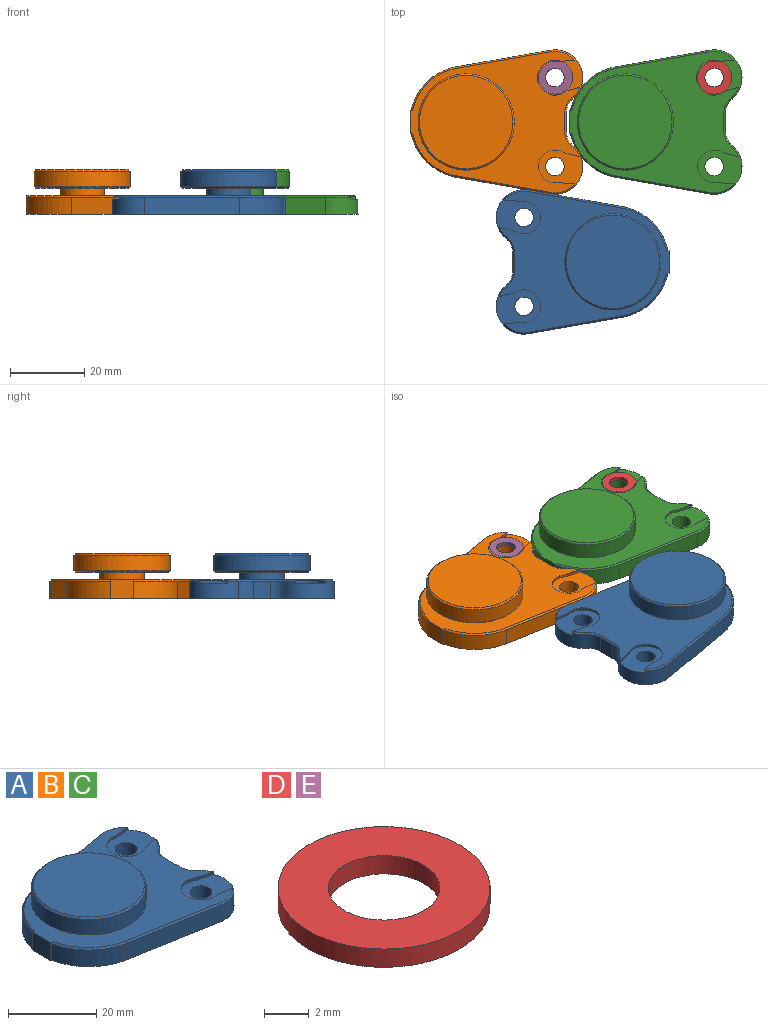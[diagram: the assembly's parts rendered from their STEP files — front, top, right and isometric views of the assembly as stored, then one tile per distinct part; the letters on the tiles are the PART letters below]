
ASSEMBLY  parts=5 mates=2
PART A: 47 faces, bbox 46.7x39x12 mm
  f0: cylinder r=13mm len=26mm, axis (0,0,-1), area 343.1mm2, adj f3,f4
  f1: plane 25.2x25.2mm, normal (0,0,1), area 498.8mm2, adj f3
  f2: plane 25.2x25.2mm, normal (0,0,-1), area 385.7mm2, adj f4,f15
  f3: cone r=12.6mm half-angle=45deg, axis (0,0,-1), area 45.5mm2, adj f0,f1
  f4: cone r=13mm half-angle=45deg, axis (0,0,1), area 45.5mm2, adj f0,f2
  f5: cylinder r=2.5mm len=5mm, axis (0,0,1), area 62.8mm2, adj f13,f25
  f6: cone r=7.1mm half-angle=45deg, axis (0,0,-1), area 4.2mm2, adj f10,f14,f18,f24,f28
  f7: plane 5x0.71mm, normal (0,1,0), area 1.6mm2, adj f8,f12,f13,f14,f17
  f8: plane 6x5mm, normal (-1,0,0), area 30mm2, adj f7,f13,f14,f31
  f9: plane 4.79x4.6mm, normal (1,0,0), area 22mm2, adj f13,f16,f21,f35
  f10: cylinder r=7.5mm len=13.26mm, axis (0,0,1), area 85.4mm2, adj f6,f11,f13,f16,f19,f23,f24,f25
  f11: plane 25.45x4.6mm, normal (-0.17,0.98,0), area 118.9mm2, adj f10,f12,f13,f18
  f12: cylinder r=15.15mm len=12.1mm, axis (0,0,1), area 82.9mm2, adj f7,f11,f13,f17
  f13: plane 46.65x39mm, normal (0,0,-1), area 1369.1mm2, adj f5,f7,f8,f9,f10,f11,f12,f16
  f14: plane 45.75x38.2mm, normal (0,0,1), area 1069.1mm2, adj f6,f7,f8,f15,f17,f18,f19,f20
  f15: cylinder r=6mm len=12mm, axis (0,0,-1), area 75.4mm2, adj f2,f14
  f16: cylinder r=5mm len=4.6mm, axis (0,0,1), area 20.2mm2, adj f9,f10,f13,f20
  f17: cone r=14.75mm half-angle=45deg, axis (0,0,-1), area 10mm2, adj f7,f12,f14,f18
  f18: plane 25.52x4.88mm, normal (-0.12,0.7,0.71), area 14.6mm2, adj f6,f11,f14,f17
  f19: cone r=7.1mm half-angle=45deg, axis (0,0,-1), area 2mm2, adj f10,f14,f20,f23,f26
  f20: cone r=5.4mm half-angle=45deg, axis (0,0,1), area 2.6mm2, adj f14,f16,f19,f21
  f21: plane 4.79x0.4mm, normal (0.71,0,0.71), area 2.7mm2, adj f9,f14,f20,f39
  f22: cylinder r=4.75mm len=9.5mm, axis (0,0,1), area 13mm2, adj f23,f24,f25,f27
  f23: plane 4.42x1.18mm, normal (-0.26,0.97,0), area 3.2mm2, adj f10,f19,f22,f25,f26
  f24: plane 4.56x0.7mm, normal (0.09,-1,0), area 3.2mm2, adj f6,f10,f22,f25,f28
  f25: plane 12.25x9.79mm, normal (0,0,1), area 76.9mm2, adj f5,f10,f22,f23,f24
  f26: plane 4.42x1.41mm, normal (-0.18,0.68,-0.71), area 1.9mm2, adj f14,f19,f23,f27
  f27: cone r=4.45mm half-angle=45deg, axis (0,0,-1), area 7.7mm2, adj f14,f22,f26,f28
  f28: plane 4.45x0.69mm, normal (0.06,-0.7,-0.71), area 1.9mm2, adj f6,f14,f24,f27
  f29: cylinder r=2.5mm len=5mm, axis (0,0,1), area 62.8mm2, adj f13,f43
  f30: cone r=7.1mm half-angle=45deg, axis (0,0,-1), area 4.2mm2, adj f14,f32,f37,f42,f46
  f31: plane 5x0.71mm, normal (0,-1,0), area 1.6mm2, adj f8,f13,f14,f34,f36
  f32: cylinder r=7.5mm len=13.26mm, axis (0,0,1), area 85.4mm2, adj f13,f30,f33,f35,f38,f41,f42,f43
  f33: plane 25.45x4.6mm, normal (-0.17,-0.98,0), area 118.9mm2, adj f13,f32,f34,f37
  f34: cylinder r=15.15mm len=12.1mm, axis (0,0,1), area 82.9mm2, adj f13,f31,f33,f36
  f35: cylinder r=5mm len=4.6mm, axis (0,0,1), area 20.2mm2, adj f9,f13,f32,f39
  f36: cone r=14.75mm half-angle=45deg, axis (0,0,-1), area 10mm2, adj f14,f31,f34,f37
  f37: plane 25.52x4.88mm, normal (-0.12,-0.7,0.71), area 14.6mm2, adj f14,f30,f33,f36
  f38: cone r=7.1mm half-angle=45deg, axis (0,0,-1), area 2mm2, adj f14,f32,f39,f41,f44
  f39: cone r=5.4mm half-angle=45deg, axis (0,0,1), area 2.6mm2, adj f14,f21,f35,f38
  f40: cylinder r=4.75mm len=9.5mm, axis (0,0,1), area 13mm2, adj f41,f42,f43,f45
  f41: plane 4.42x1.18mm, normal (-0.26,-0.97,0), area 3.2mm2, adj f32,f38,f40,f43,f44
  f42: plane 4.56x0.7mm, normal (0.09,1,0), area 3.2mm2, adj f30,f32,f40,f43,f46
  f43: plane 12.25x9.79mm, normal (0,0,1), area 76.9mm2, adj f29,f32,f40,f41,f42
  f44: plane 4.42x1.41mm, normal (-0.18,-0.68,-0.71), area 1.9mm2, adj f14,f38,f41,f45
  f45: cone r=4.45mm half-angle=45deg, axis (0,0,-1), area 7.7mm2, adj f14,f40,f44,f46
  f46: plane 4.45x0.69mm, normal (0.06,0.7,-0.71), area 1.9mm2, adj f14,f30,f42,f45
PART B: same geometry as A
PART C: same geometry as A
PART D: 4 faces, bbox 9.5x9.5x1 mm
  f0: cylinder r=2.5mm len=5mm, axis (0,0,-1), area 15.7mm2, adj f2,f3
  f1: cylinder r=4.75mm len=9.5mm, axis (0,0,-1), area 29.8mm2, adj f2,f3
  f2: plane 9.5x9.5mm, normal (0,0,1), area 51.2mm2, adj f0,f1
  f3: plane 9.5x9.5mm, normal (0,0,-1), area 51.2mm2, adj f0,f1
PART E: same geometry as D
PLACE A rot(axis=(0,0,1),180deg) t=(18.92,-52.5,-12.25)mm
PLACE B t=(-20.73,-14.75,-12.25)mm fixed
PLACE C t=(22.27,-14.75,-12.25)mm
PLACE D t=(22.27,-14.75,-12.25)mm
PLACE E t=(-20.73,-14.75,-12.25)mm
MATE fastened A.f33 <-> B.f33  axis (0.17,0.98,0) through (-0.91,-33.62,-14.95)mm
MATE fastened C.f5 <-> D.f0  axis (0,0,1) through (46.27,-2.75,-13.25)mm
